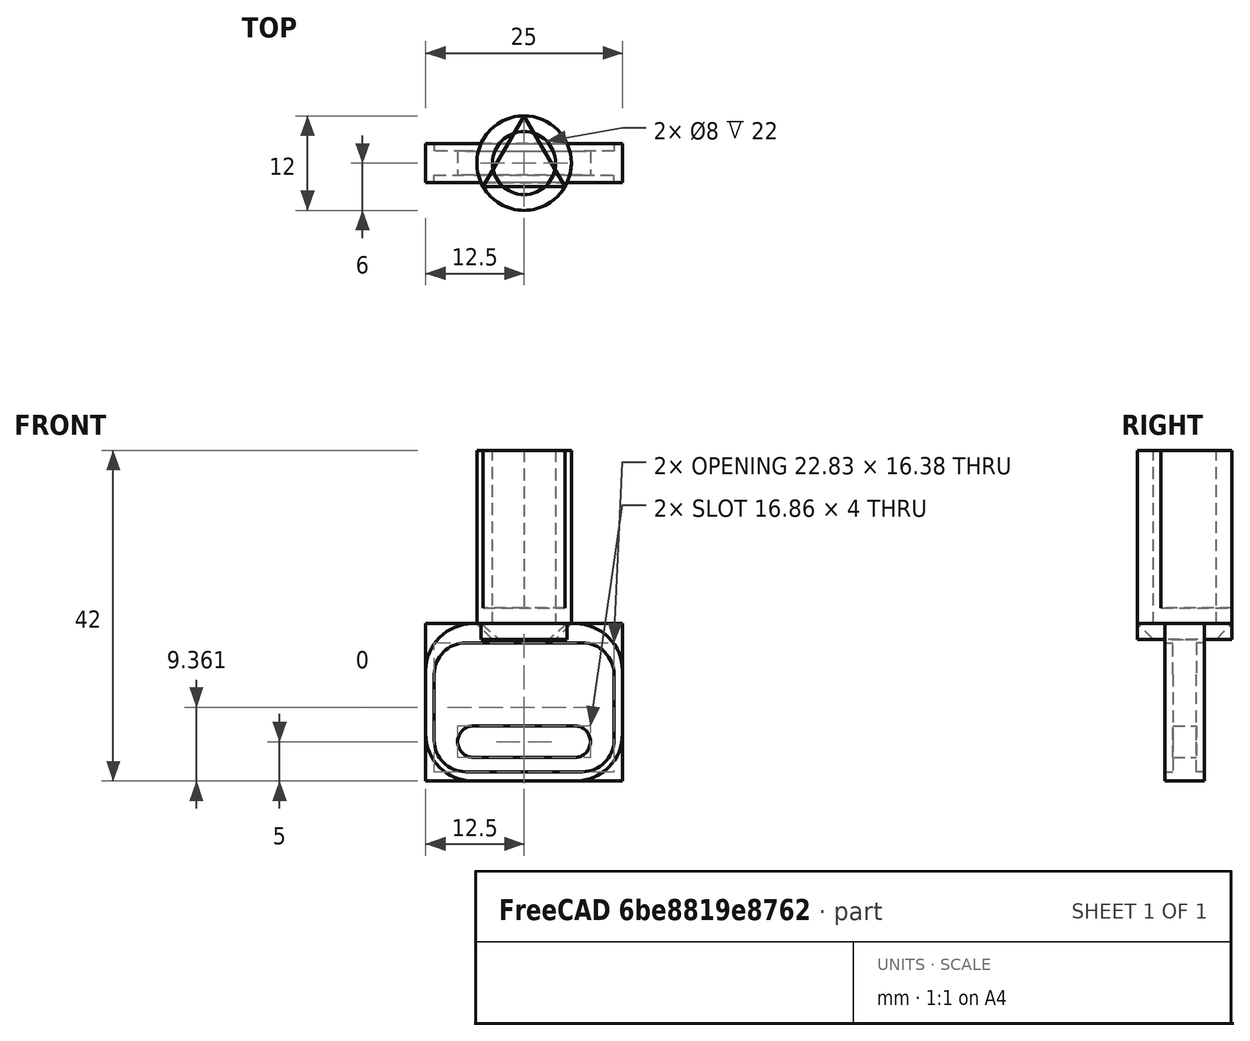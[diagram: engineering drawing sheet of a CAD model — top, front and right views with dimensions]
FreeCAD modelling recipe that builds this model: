
FCSTD DOCUMENT  (FreeCAD 0.18R14555 (Git shallow))
Label: CAME_Key
License: All rights reserved
LicenseURL: http://en.wikipedia.org/wiki/All_rights_reserved
objects: Sketcher::SketchObject×7, PartDesign::Pocket×4, PartDesign::Pad×3, PartDesign::Body×2, PartDesign::Mirrored×1, Part::Fillet×1, Part::Chamfer×1, PartDesign::Chamfer×1
note: 27 computed .brp shape members not serialized (recipe doc carries the construction recipe); baked Part::Feature solids carry a one-line shape summary decoded from their .brp

FEATURE [Sketcher::SketchObject] Sketch006  label="Handle_Sketch"
  MapMode = 5
  Support = -> [XY_Plane001]
  sketch-geometry (4):
    g0: LineSegment StartX=-12.5 StartY=2.5 StartZ=0 EndX=12.5 EndY=2.5 EndZ=0
    g1: LineSegment StartX=12.5 StartY=2.5 StartZ=0 EndX=12.5 EndY=-2.5 EndZ=0
    g2: LineSegment StartX=12.5 StartY=-2.5 StartZ=0 EndX=-12.5 EndY=-2.5 EndZ=0
    g3: LineSegment StartX=-12.5 StartY=-2.5 StartZ=0 EndX=-12.5 EndY=2.5 EndZ=0
  constraints (10):
    c: Coincident(g0,g1)
    c: Coincident(g1,g2)
    c: Coincident(g2,g3)
    c: Coincident(g3,g0)
    c: Horizontal(g2)
    c: Vertical(g3)
    c: DistanceY(g1,g1) = 5
    c: Symmetric(g1,g0,g-1)
    c: DistanceX(g0,g0) = 25
    c: Symmetric(g0,g0,g-2)
FEATURE [PartDesign::Pad] Pad  label="Handle_Pad"
  Length = 20
  Length2 = 100
  Profile = -> Sketch006
  Type = 0
FEATURE [Sketcher::SketchObject] Sketch  label="main_Sketch"
  AttachmentOffset = pos=(0,0,-2) rot=(0,0,1;0rad)
  MapMode = 5
  Placement = pos=(0,0,18) rot=(0,0,1;0rad)
  Support = -> [Pad]
  sketch-geometry (1):
    g0: Circle CenterX=0 CenterY=0 CenterZ=0 NormalX=0 NormalY=0 NormalZ=1 AngleXU=0 Radius=6
  constraints (2):
    c: Coincident(g0,g-1)
    c: Radius(g0) = 6
FEATURE [PartDesign::Pad] Pad001  label="main_Pad"
  BaseFeature = -> Pad
  Length = 24
  Length2 = 100
  Profile = -> Sketch
  Type = 0
FEATURE [Sketcher::SketchObject] Sketch001  label="InsideKey_Sketch"
  MapMode = 5
  Placement = pos=(0,0,42) rot=(0,0,1;0rad)
  Support = -> [Pad001]
  sketch-geometry (1):
    g0: Circle CenterX=0 CenterY=0 CenterZ=0 NormalX=0 NormalY=0 NormalZ=1 AngleXU=0 Radius=4
  constraints (2):
    c: Coincident(g0,g-1)
    c: Radius(g0) = 4
FEATURE [PartDesign::Pocket] Pocket001  label="inside_Pocket"
  BaseFeature = -> Pad001
  Length = 22
  Length2 = 100
  Profile = -> Sketch001
  Type = 0
FEATURE [Sketcher::SketchObject] Sketch008  label="main_Sketch003"
  AttachmentOffset = pos=(0,0,-2) rot=(0,0,1;0rad)
  MapMode = 2
  Placement = pos=(0,0,18) rot=(0,0,1;0rad)
  sketch-geometry (1):
    g0: Circle CenterX=0 CenterY=0 CenterZ=0 NormalX=0 NormalY=0 NormalZ=1 AngleXU=0 Radius=6
  constraints (2):
    c: Coincident(g0,g-1)
    c: Radius(g0) = 6
FEATURE [Sketcher::SketchObject] Sketch009
  MapMode = 5
  Placement = pos=(0,-2.5,0) rot=(1,0,0;1.5708rad)
  Support = -> [Pocket001]
  sketch-geometry (4):
    g0: ArcOfCircle CenterX=-6.43028 CenterY=5 CenterZ=0 NormalX=0 NormalY=0 NormalZ=1 AngleXU=0 Radius=2 StartAngle=1.5708 EndAngle=4.71239
    g1: ArcOfCircle CenterX=6.43028 CenterY=5 CenterZ=0 NormalX=0 NormalY=0 NormalZ=1 AngleXU=0 Radius=2 StartAngle=4.71239 EndAngle=7.85398
    g2: LineSegment StartX=-6.43028 StartY=3 StartZ=0 EndX=6.43028 EndY=3 EndZ=0
    g3: LineSegment StartX=-6.43028 StartY=7 StartZ=0 EndX=6.43028 EndY=7 EndZ=0
  constraints (8):
    c: Tangent(g0,g3) = 1.5708
    c: Tangent(g0,g2) = -1.5708
    c: Tangent(g2,g1) = -1.5708
    c: Tangent(g3,g1) = 1.5708
    c: Horizontal(g2)
    c: Symmetric(g0,g1,g-2)
    c: Radius(g1) = 2
    c: DistanceY(g-1,g1) = 3
FEATURE [PartDesign::Pocket] Pocket002
  BaseFeature = -> Pocket001
  Length = 5
  Length2 = 100
  Profile = -> Sketch009
  Type = 0
FEATURE [Sketcher::SketchObject] Sketch010
  MapMode = 5
  Placement = pos=(0,-2.5,0) rot=(1,0,0;1.5708rad)
  Support = -> [Pocket002]
  sketch-geometry (8):
    g0: LineSegment StartX=-7.41661 StartY=17.549 StartZ=0 EndX=7.41661 EndY=17.549 EndZ=0
    g1: LineSegment StartX=11.4166 StartY=13.549 StartZ=0 EndX=11.4166 EndY=5.17375 EndZ=0
    g2: LineSegment StartX=7.41661 StartY=1.17375 StartZ=0 EndX=-7.41661 EndY=1.17375 EndZ=0
    g3: LineSegment StartX=-11.4166 StartY=5.17375 StartZ=0 EndX=-11.4166 EndY=13.549 EndZ=0
    g4: ArcOfCircle CenterX=-7.41661 CenterY=13.549 CenterZ=0 NormalX=0 NormalY=0 NormalZ=1 AngleXU=0 Radius=4 StartAngle=1.5708 EndAngle=3.14159
    g5: ArcOfCircle CenterX=7.41661 CenterY=13.549 CenterZ=0 NormalX=0 NormalY=0 NormalZ=1 AngleXU=0 Radius=4 StartAngle=0 EndAngle=1.5708
    g6: ArcOfCircle CenterX=-7.41661 CenterY=5.17375 CenterZ=0 NormalX=0 NormalY=0 NormalZ=1 AngleXU=0 Radius=4 StartAngle=3.14159 EndAngle=4.71239
    g7: ArcOfCircle CenterX=7.41661 CenterY=5.17375 CenterZ=0 NormalX=0 NormalY=0 NormalZ=1 AngleXU=0 Radius=4 StartAngle=4.71239 EndAngle=6.28319
  constraints (16):
    c: Horizontal(g0)
    c: Horizontal(g2)
    c: Vertical(g1)
    c: Vertical(g3)
    c: Tangent(g0,g4) = 1.5708
    c: Tangent(g3,g4) = 1.5708
    c: Tangent(g0,g5) = 1.5708
    c: Tangent(g1,g5) = 1.5708
    c: Tangent(g3,g6) = 1.5708
    c: Tangent(g2,g6) = 1.5708
    c: Tangent(g2,g7) = 1.5708
    c: Tangent(g1,g7) = 1.5708
    c: Radius(g5) = 4
    c: Equal(g5,g4)
    c: Equal(g5,g6)
    c: Symmetric(g7,g6,g-2)
FEATURE [PartDesign::Pocket] Pocket003
  BaseFeature = -> Pocket002
  Length = 1
  Length2 = 100
  Profile = -> Sketch010
  Type = 0
FEATURE [PartDesign::Mirrored] Mirrored
  BaseFeature = -> Pocket003
  MirrorPlane = -> XZ_Plane001
  Originals = -> [Pocket003]
FEATURE [PartDesign::Body] Body001
  Group = -> [Sketch,Sketch001,Sketch006,Pad,Pad001,Pocket001,Sketch009,Pocket002,Sketch010,Pocket003,Mirrored]
  Origin = -> Origin001
  Tip = -> Mirrored
FEATURE [Part::Fillet] Fillet
  Base = -> Mirrored
  Edges = 4 edges r=6: [Edge17,Edge19,Edge21,Edge23]
FEATURE [Part::Chamfer] Chamfer
  Base = -> Fillet
  Edges = 2 edges r=2: [Edge41,Edge43]
FEATURE [PartDesign::Pad] Pad002
  Length = 24
  Length2 = 100
  Placement = pos=(0,0,18) rot=(0,0,1;0rad)
  Profile = -> Sketch008
  Type = 0
FEATURE [Sketcher::SketchObject] Sketch007  label="Triangle_Sketch001"
  MapMode = 5
  Placement = pos=(0,0,42) rot=(0,0,1;0rad)
  Support = -> [Pad002]
  sketch-geometry (4):
    g0: LineSegment StartX=5.19545 StartY=-3.00122 StartZ=0 EndX=0.00141123 EndY=6 EndZ=0
    g1: LineSegment StartX=0.00141123 StartY=6 StartZ=0 EndX=-5.19686 EndY=-2.99878 EndZ=0
    g2: LineSegment StartX=-5.19686 StartY=-2.99878 StartZ=0 EndX=5.19545 EndY=-3.00122 EndZ=0
    g3: Circle [constr] CenterX=0 CenterY=0 CenterZ=0 NormalX=0 NormalY=0 NormalZ=1 AngleXU=0 Radius=6
  constraints (10):
    c: Coincident(g0,g1)
    c: Coincident(g1,g2)
    c: Coincident(g2,g0)
    c: Equal(g0,g1)
    c: Equal(g0,g2)
    c: PointOnObject(g0,g3)
    c: PointOnObject(g1,g3)
    c: PointOnObject(g2,g3)
    c: Coincident(g3,g-1)
    c: Radius(g3) = 6
FEATURE [PartDesign::Pocket] Pocket
  BaseFeature = -> Pad002
  Length = 20
  Length2 = 100
  Placement = pos=(0,0,18) rot=(0,0,1;0rad)
  Profile = -> Sketch007
  Type = 0
FEATURE [PartDesign::Chamfer] Chamfer001
  Base = -> Pocket [Edge1]
  BaseFeature = -> Pocket
  Placement = pos=(0,0,18) rot=(0,0,1;0rad)
  Size = 2
FEATURE [PartDesign::Body] Body
  Group = -> [Sketch007,Sketch008,Pad002,Pocket,Chamfer001]
  Origin = -> Origin
  Tip = -> Chamfer001
